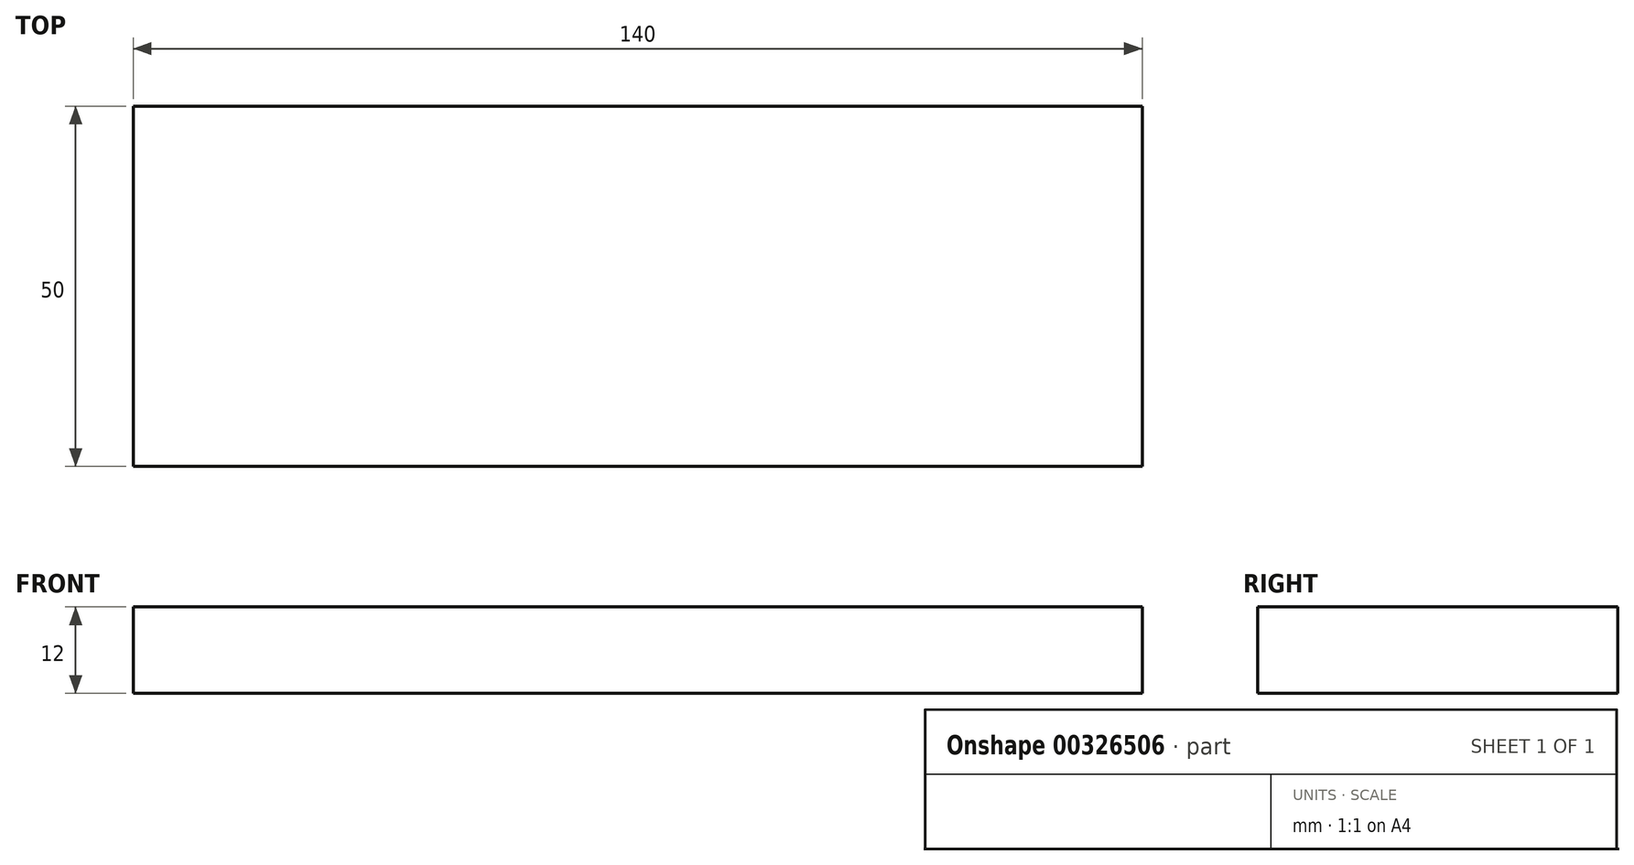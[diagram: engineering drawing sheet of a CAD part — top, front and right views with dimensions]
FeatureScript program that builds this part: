
annotation { "Feature Type Name" : "Feature", "Feature Type Description" : "" }
export const myFeature = defineFeature(function(context is Context, id is Id, definition is map)
    precondition{}
    {
        {
            var Q0;
            Q0=qCreatedBy(makeId("Top.planeOp"),FACE);
            var sketch = newSketch(context, id + "F0", { "sketchPlane" : qUnion([Q0])});
            skLineSegment(sketch, "E0", {"start": v(-65.04, -40.42) * mm, "end": v(74.96, -40.42) * mm});
            skLineSegment(sketch, "E1", {"start": v(74.96, -40.42) * mm, "end": v(74.96, 9.58) * mm});
            skLineSegment(sketch, "E2", {"start": v(74.96, 9.58) * mm, "end": v(-65.04, 9.58) * mm});
            skLineSegment(sketch, "E3", {"start": v(-65.04, 9.58) * mm, "end": v(-65.04, -40.42) * mm});
            skSolve(sketch);
        }
        {
            var Q0;
            Q0=makeQuery(id+"F0.imprint","IMPRINT",FACE,{"disambiguationData":[TD([[makeQuery(id+"F0.imprint","IMPRINT",EDGE,{"derivedFrom":sQuery(id+"F0.wireOp",EDGE,"E0")}),1.0]])]});
            extrude(context, id + "F1", {"entities" : qUnion([Q0]), "depth" : 12 * mm});
        }
    });
